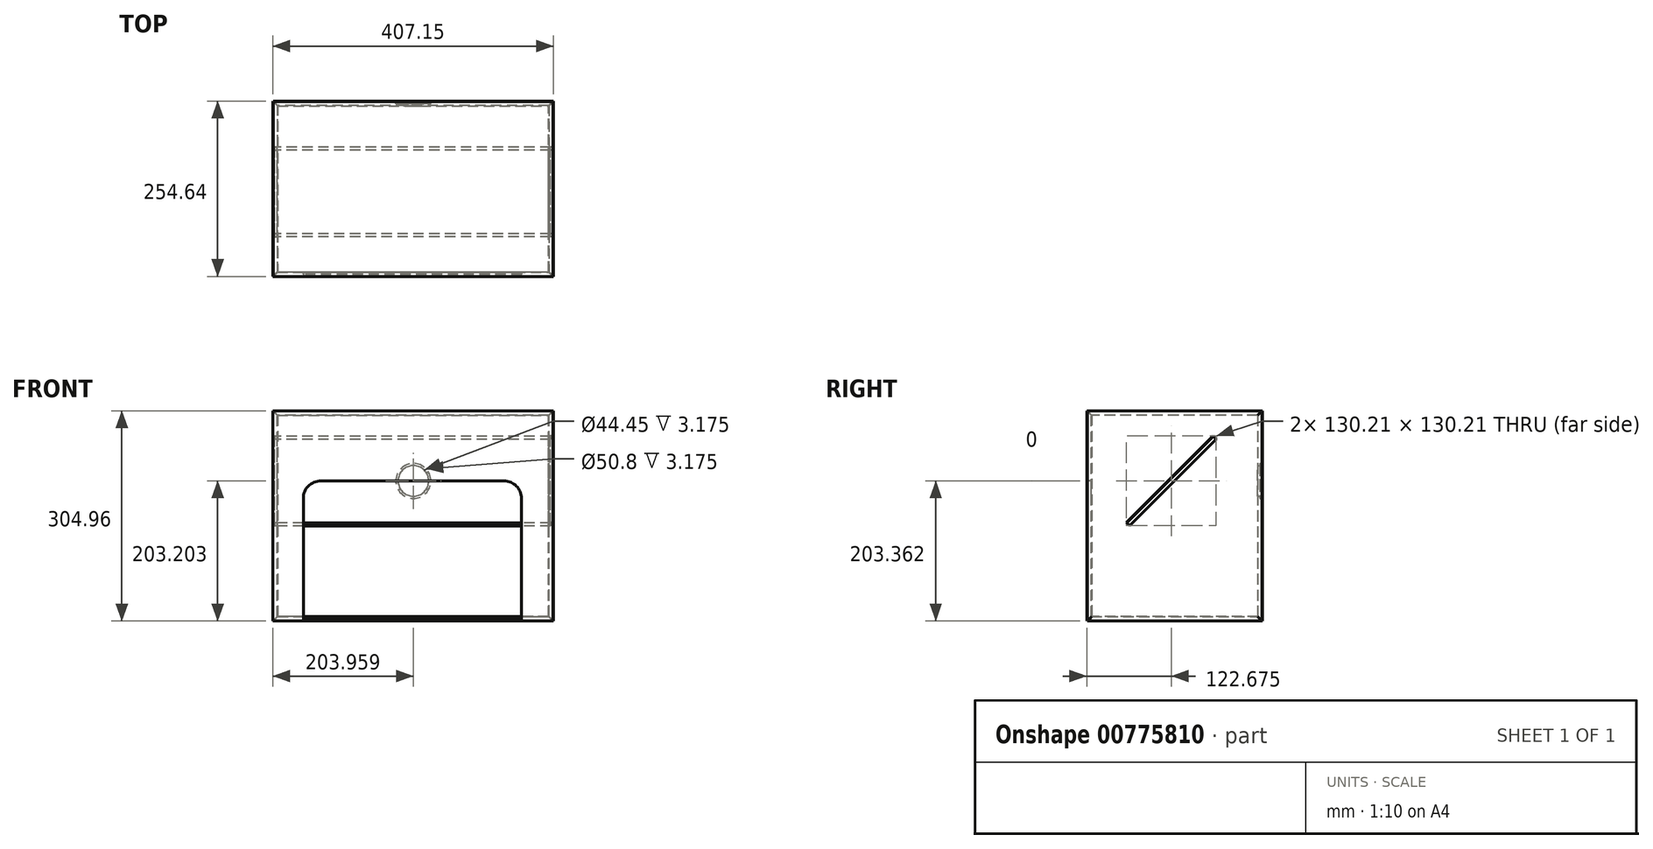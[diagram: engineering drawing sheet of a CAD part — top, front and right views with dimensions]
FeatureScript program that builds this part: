
annotation { "Feature Type Name" : "Feature", "Feature Type Description" : "" }
export const myFeature = defineFeature(function(context is Context, id is Id, definition is map)
    precondition{}
    {
        {
            var Q0;
            Q0=qCreatedBy(makeId("Top.planeOp"),FACE);
            var sketch = newSketch(context, id + "F0", { "sketchPlane" : qUnion([Q0])});
            skLineSegment(sketch, "E0.bottom", {"start": v(-199.1, 158) * mm, "end": v(207.3, 158) * mm});
            skLineSegment(sketch, "E0.top", {"start": v(-199.1, -96) * mm, "end": v(207.3, -96) * mm});
            skLineSegment(sketch, "E0.left", {"start": v(-199.1, 158) * mm, "end": v(-199.1, -96) * mm});
            skLineSegment(sketch, "E0.right", {"start": v(207.3, 158) * mm, "end": v(207.3, -96) * mm});
            skSolve(sketch);
        }
        {
            var Q0;
            Q0=makeQuery(id+"F0.imprint","IMPRINT",FACE,{"disambiguationData":[TD([[makeQuery(id+"F0.imprint","IMPRINT",EDGE,{"derivedFrom":sQuery(id+"F0.wireOp",EDGE,"E0.bottom")}),-1.0]])]});
            extrude(context, id + "F1", {"entities" : qUnion([Q0]), "depth" : 6.35 * mm, "offsetDistance" : 25.4 * mm});
        }
        {
            var Q0;
            Q0=makeQuery(id+"F1.opExtrude","CAP_EDGE",EDGE,{"disambiguationData":[OSD([sQuery(id+"F0.wireOp",EDGE,"E0.left")])],"isStart":false});
            var Q1;
            Q1=makeQuery(id+"F1.opExtrude","CAP_FACE",FACE,{"disambiguationData":[OSD([sQuery(id+"F0.wireOp",EDGE,"E0.bottom"),sQuery(id+"F0.wireOp",EDGE,"E0.top"),sQuery(id+"F0.wireOp",EDGE,"E0.left"),sQuery(id+"F0.wireOp",EDGE,"E0.right")])],"isStart":false});
            var Q2;
            Q2=makeQuery(id+"F1.opExtrude","CAP_EDGE",EDGE,{"disambiguationData":[OSD([sQuery(id+"F0.wireOp",EDGE,"E0.bottom")])],"isStart":false});
            var Q3;
            Q3=makeQuery(id+"F1.opExtrude","CAP_EDGE",EDGE,{"disambiguationData":[OSD([sQuery(id+"F0.wireOp",EDGE,"E0.right")])],"isStart":false});
            chamfer(context, id + "F2", {"entities" : qUnion([Q0, Q1, Q2, Q3]), "width" : 6.35 * mm, "tangentPropagation" : true});
        }
        {
            var Q0;
            Q0=qCreatedBy(makeId("Front.planeOp"),FACE);
            var sketch = newSketch(context, id + "F3", { "sketchPlane" : qUnion([Q0])});
            skLineSegment(sketch, "E1.bottom", {"start": v(-118.82, 429.1) * mm, "end": v(287.58, 429.1) * mm});
            skLineSegment(sketch, "E1.top", {"start": v(-118.82, 124.3) * mm, "end": v(287.58, 124.3) * mm});
            skLineSegment(sketch, "E1.left", {"start": v(-118.82, 429.1) * mm, "end": v(-118.82, 124.3) * mm});
            skLineSegment(sketch, "E1.right", {"start": v(287.58, 429.1) * mm, "end": v(287.58, 124.3) * mm});
            skSolve(sketch);
        }
        {
            var Q0;
            Q0=makeQuery(id+"F3.imprint","IMPRINT",FACE,{"disambiguationData":[TD([[makeQuery(id+"F3.imprint","IMPRINT",EDGE,{"derivedFrom":sQuery(id+"F3.wireOp",EDGE,"E1.bottom")}),-1.0]])]});
            extrude(context, id + "F4", {"entities" : qUnion([Q0]), "depth" : 6.35 * mm, "offsetDistance" : 25.4 * mm});
        }
        {
            var Q0;
            Q0=makeQuery(id+"F4.opExtrude","CAP_EDGE",EDGE,{"disambiguationData":[OSD([sQuery(id+"F3.wireOp",EDGE,"E1.top")])],"isStart":false});
            var Q1;
            Q1=makeQuery(id+"F4.opExtrude","CAP_EDGE",EDGE,{"disambiguationData":[OSD([sQuery(id+"F3.wireOp",EDGE,"E1.right")])],"isStart":false});
            var Q2;
            Q2=makeQuery(id+"F4.opExtrude","CAP_EDGE",EDGE,{"disambiguationData":[OSD([sQuery(id+"F3.wireOp",EDGE,"E1.left")])],"isStart":false});
            var Q3;
            Q3=makeQuery(id+"F4.opExtrude","CAP_EDGE",EDGE,{"disambiguationData":[OSD([sQuery(id+"F3.wireOp",EDGE,"E1.bottom")])],"isStart":false});
            chamfer(context, id + "F5", {"entities" : qUnion([Q0, Q1, Q2, Q3]), "width" : 6.35 * mm, "tangentPropagation" : true});
        }
        {
            var Q0;
            Q0=makeQuery(id+"F4.opExtrude","CAP_FACE",FACE,{"disambiguationData":[OSD([sQuery(id+"F3.wireOp",EDGE,"E1.bottom"),sQuery(id+"F3.wireOp",EDGE,"E1.top"),sQuery(id+"F3.wireOp",EDGE,"E1.left"),sQuery(id+"F3.wireOp",EDGE,"E1.right")])],"isStart":true});
            var sketch = newSketch(context, id + "F6", { "sketchPlane" : qUnion([Q0])});
            skPoint(sketch, "E2", {"position": v(-84.39, 327.5) * mm});
            skSolve(sketch);
        }
        {
            var Q0;
            Q0=sQuery(id+"F6.wireOp",VERTEX,"E2");
            var Q1;
            Q1=makeQuery(id+"F4.opExtrude","SWEPT_BODY",BODY,{"disambiguationData":[OSD([sQuery(id+"F3.wireOp",EDGE,"E1.bottom"),sQuery(id+"F3.wireOp",EDGE,"E1.top"),sQuery(id+"F3.wireOp",EDGE,"E1.left"),sQuery(id+"F3.wireOp",EDGE,"E1.right")])]});
            hole(context, id + "F7", {"style" : HoleStyle.C_BORE, "endStyle" : HoleEndStyle.THROUGH, "holeDiameter" : 44.45 * mm, "cBoreDiameter" : 50.8 * mm, "cBoreDepth" : 3.17 * mm, "majorDiameter" : 6.35 * mm, "isTappedThrough" : true, "tappedDepth" : 12.7 * mm, "tapClearance" : 3, "locations" : qUnion([Q0]), "scope" : qUnion([Q1])});
        }
        {
            var Q0;
            Q0=qCreatedBy(makeId("Right.planeOp"),FACE);
            var sketch = newSketch(context, id + "F8", { "sketchPlane" : qUnion([Q0])});
            skLineSegment(sketch, "E3.bottom", {"start": v(-236.32, 132.56) * mm, "end": v(-43.57, 132.56) * mm});
            skLineSegment(sketch, "E3.top", {"start": v(-236.32, 138.95) * mm, "end": v(-43.57, 138.95) * mm});
            skLineSegment(sketch, "E3.left", {"start": v(-236.32, 132.56) * mm, "end": v(-236.32, 138.95) * mm});
            skLineSegment(sketch, "E3.right", {"start": v(-43.57, 132.56) * mm, "end": v(-43.57, 138.95) * mm});
            skSolve(sketch);
        }
        {
            var Q0;
            Q0 = qSketchRegion(id + "F8", true);
            extrude(context, id + "F9", {"entities" : qUnion([Q0]), "depth" : 355.6 * mm, "offsetDistance" : 25.4 * mm});
        }
        {
            var Q0;
            Q0=makeQuery(id+"F9.opExtrude","SWEPT_BODY",BODY,{"disambiguationData":[OSD([sQuery(id+"F8.wireOp",EDGE,"E3.bottom"),sQuery(id+"F8.wireOp",EDGE,"E3.top"),sQuery(id+"F8.wireOp",EDGE,"E3.left"),sQuery(id+"F8.wireOp",EDGE,"E3.right")])]});
            var Q1;
            Q1=makeQuery(id+"F9.opExtrude","SWEPT_EDGE",EDGE,{"disambiguationData":[OSD([sQuery(id+"F8.wireOp",EDGE,"E3.bottom"),sQuery(id+"F8.wireOp",EDGE,"E3.left")])]});
            transform(context, id + "F10", {"entities" : qUnion([Q0]), "transformType" : TransformType.ROTATION, "transformAxis" : qUnion([Q1]), "angle" : 45 * degree, "oppositeDirection" : true, "makeCopy" : false});
        }
        {
            var Q0;
            Q0=makeQuery(id+"F9.opExtrude","SWEPT_BODY",BODY,{"disambiguationData":[OSD([sQuery(id+"F8.wireOp",EDGE,"E3.bottom"),sQuery(id+"F8.wireOp",EDGE,"E3.top"),sQuery(id+"F8.wireOp",EDGE,"E3.left"),sQuery(id+"F8.wireOp",EDGE,"E3.right")])]});
            var Q1;
            Q1=qCreatedBy(makeId("Right.planeOp"),FACE);
            transform(context, id + "F11", {"entities" : qUnion([Q0]), "transformType" : TransformType.TRANSLATION_DISTANCE, "transformDirection" : qUnion([Q1]), "distance" : 101.6 * mm, "oppositeDirection" : true, "makeCopy" : false});
        }
        {
            var Q0;
            Q0=makeQuery(id+"F9.opExtrude","SWEPT_BODY",BODY,{"disambiguationData":[OSD([sQuery(id+"F8.wireOp",EDGE,"E3.bottom"),sQuery(id+"F8.wireOp",EDGE,"E3.top"),sQuery(id+"F8.wireOp",EDGE,"E3.left"),sQuery(id+"F8.wireOp",EDGE,"E3.right")])]});
            var Q1;
            Q1=makeQuery(id+"F9.opExtrude","SWEPT_FACE",FACE,{"disambiguationData":[OSD([sQuery(id+"F8.wireOp",EDGE,"E3.top")])]});
            transform(context, id + "F12", {"entities" : qUnion([Q0]), "transformType" : TransformType.TRANSLATION_DISTANCE, "transformDirection" : qUnion([Q1]), "distance" : 101.6 * mm, "makeCopy" : false});
        }
        {
            var Q0;
            Q0=makeQuery(id+"F9.opExtrude","CAP_EDGE",EDGE,{"disambiguationData":[OSD([sQuery(id+"F8.wireOp",EDGE,"E3.bottom")])],"isStart":false});
            var Q1;
            Q1=makeQuery(id+"F9.opExtrude","CAP_EDGE",EDGE,{"disambiguationData":[OSD([sQuery(id+"F8.wireOp",EDGE,"E3.top")])],"isStart":false});
            chamfer(context, id + "F13", {"entities" : qUnion([Q0, Q1]), "width" : 2.54 * mm, "tangentPropagation" : true});
        }
        {
            var Q0;
            Q0=makeQuery(id+"F4.opExtrude","SWEPT_BODY",BODY,{"disambiguationData":[OSD([sQuery(id+"F3.wireOp",EDGE,"E1.bottom"),sQuery(id+"F3.wireOp",EDGE,"E1.top"),sQuery(id+"F3.wireOp",EDGE,"E1.left"),sQuery(id+"F3.wireOp",EDGE,"E1.right")])]});
            transform(context, id + "F14", {"entities" : qUnion([Q0]), "transformType" : TransformType.TRANSLATION_3D, "dx" : 0 * mm, "dy" : 152.4 * mm, "dz" : -127 * mm, "makeCopy" : false});
        }
        {
            var Q0;
            Q0=makeQuery(id+"F1.opExtrude","SWEPT_BODY",BODY,{"disambiguationData":[OSD([sQuery(id+"F0.wireOp",EDGE,"E0.bottom"),sQuery(id+"F0.wireOp",EDGE,"E0.top"),sQuery(id+"F0.wireOp",EDGE,"E0.left"),sQuery(id+"F0.wireOp",EDGE,"E0.right")])]});
            transform(context, id + "F15", {"entities" : qUnion([Q0]), "transformType" : TransformType.TRANSLATION_3D, "dx" : 0 * mm, "dy" : -5.08 * mm, "dz" : -2.54 * mm, "makeCopy" : false});
        }
        {
            var Q0;
            Q0=makeQuery(id+"F4.opExtrude","SWEPT_BODY",BODY,{"disambiguationData":[OSD([sQuery(id+"F3.wireOp",EDGE,"E1.bottom"),sQuery(id+"F3.wireOp",EDGE,"E1.top"),sQuery(id+"F3.wireOp",EDGE,"E1.left"),sQuery(id+"F3.wireOp",EDGE,"E1.right")])]});
            transform(context, id + "F16", {"entities" : qUnion([Q0]), "transformType" : TransformType.TRANSLATION_3D, "dx" : -80 * mm, "dy" : 0 * mm, "dz" : 0 * mm, "makeCopy" : false});
        }
        {
            var Q0;
            Q0=qCreatedBy(makeId("Right.planeOp"),FACE);
            var sketch = newSketch(context, id + "F17", { "sketchPlane" : qUnion([Q0])});
            skLineSegment(sketch, "E4.bottom", {"start": v(153.04, 0) * mm, "end": v(-100.96, 0) * mm});
            skLineSegment(sketch, "E4.top", {"start": v(153.04, 304.8) * mm, "end": v(-100.96, 304.8) * mm});
            skLineSegment(sketch, "E4.left", {"start": v(153.04, 0) * mm, "end": v(153.04, 304.8) * mm});
            skLineSegment(sketch, "E4.right", {"start": v(-100.96, 0) * mm, "end": v(-100.96, 304.8) * mm});
            skSolve(sketch);
        }
        {
            var Q0;
            Q0=makeQuery(id+"F17.imprint","IMPRINT",FACE,{"disambiguationData":[TD([[makeQuery(id+"F17.imprint","IMPRINT",EDGE,{"derivedFrom":sQuery(id+"F17.wireOp",EDGE,"E4.bottom")}),-1.0]])]});
            extrude(context, id + "F18", {"entities" : qUnion([Q0]), "depth" : 6.35 * mm, "offsetDistance" : 25.4 * mm});
        }
        {
            var Q0;
            Q0=makeQuery(id+"F18.opExtrude","SWEPT_BODY",BODY,{"disambiguationData":[OSD([sQuery(id+"F17.wireOp",EDGE,"E4.bottom"),sQuery(id+"F17.wireOp",EDGE,"E4.top"),sQuery(id+"F17.wireOp",EDGE,"E4.left"),sQuery(id+"F17.wireOp",EDGE,"E4.right")])]});
            transform(context, id + "F19", {"entities" : qUnion([Q0]), "transformType" : TransformType.TRANSLATION_3D, "dx" : -199.39 * mm, "dy" : 0 * mm, "dz" : -2.54 * mm, "makeCopy" : false});
        }
        {
            var Q0;
            Q0=makeQuery(id+"F18.opExtrude","CAP_EDGE",EDGE,{"disambiguationData":[OSD([sQuery(id+"F17.wireOp",EDGE,"E4.bottom")])],"isStart":false});
            var Q1;
            Q1=makeQuery(id+"F18.opExtrude","CAP_EDGE",EDGE,{"disambiguationData":[OSD([sQuery(id+"F17.wireOp",EDGE,"E4.right")])],"isStart":false});
            var Q2;
            Q2=makeQuery(id+"F18.opExtrude","CAP_EDGE",EDGE,{"disambiguationData":[OSD([sQuery(id+"F17.wireOp",EDGE,"E4.left")])],"isStart":false});
            var Q3;
            Q3=makeQuery(id+"F18.opExtrude","CAP_EDGE",EDGE,{"disambiguationData":[OSD([sQuery(id+"F17.wireOp",EDGE,"E4.top")])],"isStart":false});
            chamfer(context, id + "F20", {"entities" : qUnion([Q0, Q1, Q2, Q3]), "width" : 6.35 * mm, "tangentPropagation" : true});
        }
        {
            var Q0;
            Q0=qCreatedBy(makeId("Right.planeOp"),FACE);
            var sketch = newSketch(context, id + "F21", { "sketchPlane" : qUnion([Q0])});
            skLineSegment(sketch, "E5.bottom", {"start": v(-47.49, 150.59) * mm, "end": v(78.24, 276.31) * mm});
            skLineSegment(sketch, "E5.top", {"start": v(-43, 146.1) * mm, "end": v(82.73, 271.82) * mm});
            skLineSegment(sketch, "E5.left", {"start": v(-47.49, 150.59) * mm, "end": v(-43, 146.1) * mm});
            skLineSegment(sketch, "E5.right", {"start": v(78.24, 276.31) * mm, "end": v(82.73, 271.82) * mm});
            skSolve(sketch);
        }
        {
            var Q0;
            Q0 = qSketchRegion(id + "F21", true);
            extrude(context, id + "F22", {"entities" : qUnion([Q0]), "depth" : 400.05 * mm, "offsetDistance" : 25.4 * mm});
        }
        {
            var Q0;
            Q0=makeQuery(id+"F18.opExtrude","CAP_FACE",FACE,{"disambiguationData":[OSD([sQuery(id+"F17.wireOp",EDGE,"E4.bottom"),sQuery(id+"F17.wireOp",EDGE,"E4.top"),sQuery(id+"F17.wireOp",EDGE,"E4.left"),sQuery(id+"F17.wireOp",EDGE,"E4.right")])],"isStart":false});
            var sketch = newSketch(context, id + "F23", { "sketchPlane" : qUnion([Q0])});
            skLineSegment(sketch, "E6.bottom", {"start": v(-44.03, 140.05) * mm, "end": v(81.7, 265.77) * mm});
            skLineSegment(sketch, "E6.top", {"start": v(-39.54, 135.56) * mm, "end": v(86.18, 261.28) * mm});
            skLineSegment(sketch, "E6.left", {"start": v(-44.03, 140.05) * mm, "end": v(-39.54, 135.56) * mm});
            skLineSegment(sketch, "E6.right", {"start": v(81.7, 265.77) * mm, "end": v(86.18, 261.28) * mm});
            skSolve(sketch);
        }
        {
            var Q0;
            Q0 = qSketchRegion(id + "F23", true);
            extrude(context, id + "F24", {"entities" : qUnion([Q0]), "operationType" : NewBodyOperationType.REMOVE, "oppositeDirection" : true, "depth" : 3.17 * mm, "offsetDistance" : 25.4 * mm});
        }
        {
            var Q0;
            Q0=makeQuery(id+"F22.opExtrude","SWEPT_FACE",FACE,{"disambiguationData":[OSD([sQuery(id+"F21.wireOp",EDGE,"E5.top")])]});
            var sketch = newSketch(context, id + "F25", { "sketchPlane" : qUnion([Q0])});
            skLineSegment(sketch, "E7.bottom", {"start": v(25.4, -98.32) * mm, "end": v(374.65, -98.32) * mm});
            skLineSegment(sketch, "E7.top", {"start": v(25.4, -225.32) * mm, "end": v(374.65, -225.32) * mm});
            skLineSegment(sketch, "E7.left", {"start": v(25.4, -98.32) * mm, "end": v(25.4, -225.32) * mm});
            skLineSegment(sketch, "E7.right", {"start": v(374.65, -98.32) * mm, "end": v(374.65, -225.32) * mm});
            skPoint(sketch, "E7.middle", {"position": v(207.97, -188.2) * mm});
            skSolve(sketch);
        }
        {
            var Q0;
            Q0=makeQuery(id+"F25.imprint","IMPRINT",FACE,{"disambiguationData":[TD([[makeQuery(id+"F25.imprint","IMPRINT",EDGE,{"derivedFrom":sQuery(id+"F25.wireOp",EDGE,"E7.bottom")}),-1.0]])]});
            extrude(context, id + "F26", {"entities" : qUnion([Q0]), "operationType" : NewBodyOperationType.REMOVE, "oppositeDirection" : true, "depth" : 3.17 * mm, "offsetDistance" : 25.4 * mm});
        }
        {
            var Q0;
            Q0=makeQuery(id+"F18.opExtrude","SWEPT_BODY",BODY,{"disambiguationData":[OSD([sQuery(id+"F17.wireOp",EDGE,"E4.bottom"),sQuery(id+"F17.wireOp",EDGE,"E4.top"),sQuery(id+"F17.wireOp",EDGE,"E4.left"),sQuery(id+"F17.wireOp",EDGE,"E4.right")])]});
            transform(context, id + "F27", {"entities" : qUnion([Q0]), "transformType" : TransformType.TRANSLATION_3D, "dx" : 0 * mm, "dy" : 0 * mm, "dz" : 0 * mm, "makeCopy" : true});
        }
        {
            var Q0;
            Q0=makeQuery(id+"F27.opPattern","COPY",BODY,{"derivedFrom":makeQuery(id+"F18.opExtrude","SWEPT_BODY",BODY,{"disambiguationData":[OSD([sQuery(id+"F17.wireOp",EDGE,"E4.bottom"),sQuery(id+"F17.wireOp",EDGE,"E4.top"),sQuery(id+"F17.wireOp",EDGE,"E4.left"),sQuery(id+"F17.wireOp",EDGE,"E4.right")])]}),"instanceName":"1"});
            deleteBodies(context, id + "F28", {"entities" : qUnion([Q0])});
        }
        {
            var Q0;
            Q0 = qSketchRegion(id + "F23", true);
            extrude(context, id + "F29", {"entities" : qUnion([Q0]), "operationType" : NewBodyOperationType.REMOVE, "oppositeDirection" : true, "depth" : 25.4 * mm, "offsetDistance" : 25.4 * mm});
        }
        {
            var Q0;
            Q0=qCreatedBy(makeId("Front.planeOp"),FACE);
            var sketch = newSketch(context, id + "F30", { "sketchPlane" : qUnion([Q0])});
            skLineSegment(sketch, "E8.bottom", {"start": v(209.36, 0) * mm, "end": v(-197.04, 0) * mm});
            skLineSegment(sketch, "E8.top", {"start": v(209.36, 304.8) * mm, "end": v(-197.04, 304.8) * mm});
            skLineSegment(sketch, "E8.left", {"start": v(209.36, 0) * mm, "end": v(209.36, 304.8) * mm});
            skLineSegment(sketch, "E8.right", {"start": v(-197.04, 0) * mm, "end": v(-197.04, 304.8) * mm});
            skSolve(sketch);
        }
        {
            var Q0;
            Q0=makeQuery(id+"F30.imprint","IMPRINT",FACE,{"disambiguationData":[TD([[makeQuery(id+"F30.imprint","IMPRINT",EDGE,{"derivedFrom":sQuery(id+"F30.wireOp",EDGE,"E8.bottom")}),-1.0]])]});
            extrude(context, id + "F31", {"entities" : qUnion([Q0]), "depth" : 6.35 * mm, "offsetDistance" : 25.4 * mm});
        }
        {
            var Q0;
            Q0=makeQuery(id+"F31.opExtrude","CAP_EDGE",EDGE,{"disambiguationData":[OSD([sQuery(id+"F30.wireOp",EDGE,"E8.left")])],"isStart":true});
            var Q1;
            Q1=makeQuery(id+"F31.opExtrude","CAP_EDGE",EDGE,{"disambiguationData":[OSD([sQuery(id+"F30.wireOp",EDGE,"E8.bottom")])],"isStart":true});
            var Q2;
            Q2=makeQuery(id+"F31.opExtrude","CAP_EDGE",EDGE,{"disambiguationData":[OSD([sQuery(id+"F30.wireOp",EDGE,"E8.right")])],"isStart":true});
            var Q3;
            Q3=makeQuery(id+"F31.opExtrude","CAP_EDGE",EDGE,{"disambiguationData":[OSD([sQuery(id+"F30.wireOp",EDGE,"E8.top")])],"isStart":true});
            chamfer(context, id + "F32", {"entities" : qUnion([Q0, Q1, Q2, Q3]), "width" : 6.35 * mm, "tangentPropagation" : true});
        }
        {
            var Q0;
            Q0=makeQuery(id+"F31.opExtrude","SWEPT_BODY",BODY,{"disambiguationData":[OSD([sQuery(id+"F30.wireOp",EDGE,"E8.bottom"),sQuery(id+"F30.wireOp",EDGE,"E8.top"),sQuery(id+"F30.wireOp",EDGE,"E8.left"),sQuery(id+"F30.wireOp",EDGE,"E8.right")])]});
            transform(context, id + "F33", {"entities" : qUnion([Q0]), "transformType" : TransformType.TRANSLATION_3D, "dx" : -2.54 * mm, "dy" : -95.25 * mm, "dz" : 0 * mm, "makeCopy" : false});
        }
        {
            var Q0;
            Q0=makeQuery(id+"F31.opExtrude","CAP_FACE",FACE,{"disambiguationData":[OSD([sQuery(id+"F30.wireOp",EDGE,"E8.bottom"),sQuery(id+"F30.wireOp",EDGE,"E8.top"),sQuery(id+"F30.wireOp",EDGE,"E8.left"),sQuery(id+"F30.wireOp",EDGE,"E8.right")])],"isStart":false});
            var sketch = newSketch(context, id + "F34", { "sketchPlane" : qUnion([Q0])});
            skLineSegment(sketch, "E9", {"start": v(-155.34, 0) * mm, "end": v(-155.34, 177.8) * mm});
            skLineSegment(sketch, "E10", {"start": v(161.17, 177.8) * mm, "end": v(161.17, 0) * mm});
            skLineSegment(sketch, "E11", {"start": v(161.17, 0) * mm, "end": v(-155.34, 0) * mm});
            skLineSegment(sketch, "E12", {"start": v(-129.94, 203.2) * mm, "end": v(135.77, 203.2) * mm});
            skPoint(sketch, "E13.visualSharp", {"position": v(-155.34, 203.2) * mm});
            skArc(sketch, "E13.filletArc", {"start": v(-129.94, 203.2) * mm, "mid": v(-147.9, 195.76) * mm, "end": v(-155.34, 177.8) * mm});
            skPoint(sketch, "E14.visualSharp", {"position": v(161.17, 203.2) * mm});
            skArc(sketch, "E14.filletArc", {"start": v(161.17, 177.8) * mm, "mid": v(153.73, 195.76) * mm, "end": v(135.77, 203.2) * mm});
            skSolve(sketch);
        }
        {
            var Q0;
            Q0=makeQuery(id+"F34.imprint","IMPRINT",FACE,{"disambiguationData":[TD([[makeQuery(id+"F34.imprint","IMPRINT",EDGE,{"derivedFrom":sQuery(id+"F34.wireOp",EDGE,"E9")}),-1.0]])]});
            extrude(context, id + "F35", {"entities" : qUnion([Q0]), "operationType" : NewBodyOperationType.REMOVE, "oppositeDirection" : true, "depth" : 6.35 * mm, "offsetDistance" : 25.4 * mm});
        }
        {
            var Q0;
            Q0=makeQuery(id+"F9.opExtrude","SWEPT_BODY",BODY,{"disambiguationData":[OSD([sQuery(id+"F8.wireOp",EDGE,"E3.bottom"),sQuery(id+"F8.wireOp",EDGE,"E3.top"),sQuery(id+"F8.wireOp",EDGE,"E3.left"),sQuery(id+"F8.wireOp",EDGE,"E3.right")])]});
            deleteBodies(context, id + "F36", {"entities" : qUnion([Q0])});
        }
        {
            var Q0;
            Q0=makeQuery(id+"F22.opExtrude","SWEPT_BODY",BODY,{"disambiguationData":[OSD([sQuery(id+"F21.wireOp",EDGE,"E5.bottom"),sQuery(id+"F21.wireOp",EDGE,"E5.top"),sQuery(id+"F21.wireOp",EDGE,"E5.left"),sQuery(id+"F21.wireOp",EDGE,"E5.right")])]});
            transform(context, id + "F37", {"entities" : qUnion([Q0]), "transformType" : TransformType.TRANSLATION_3D, "dx" : -196.85 * mm, "dy" : 3.56 * mm, "dz" : -11.18 * mm, "makeCopy" : false});
        }
        {
            var Q0;
            Q0=makeQuery(id+"F31.opExtrude","SWEPT_BODY",BODY,{"disambiguationData":[OSD([sQuery(id+"F30.wireOp",EDGE,"E8.bottom"),sQuery(id+"F30.wireOp",EDGE,"E8.top"),sQuery(id+"F30.wireOp",EDGE,"E8.left"),sQuery(id+"F30.wireOp",EDGE,"E8.right")])]});
            transform(context, id + "F38", {"entities" : qUnion([Q0]), "transformType" : TransformType.TRANSLATION_3D, "dx" : 0 * mm, "dy" : 0 * mm, "dz" : -2.54 * mm, "makeCopy" : false});
        }
        {
            var Q0;
            Q0=qCreatedBy(makeId("Top.planeOp"),FACE);
            var sketch = newSketch(context, id + "F39", { "sketchPlane" : qUnion([Q0])});
            skLineSegment(sketch, "E15.bottom", {"start": v(-198.61, 151.65) * mm, "end": v(207.79, 151.65) * mm});
            skLineSegment(sketch, "E15.top", {"start": v(-198.61, -102.35) * mm, "end": v(207.79, -102.35) * mm});
            skLineSegment(sketch, "E15.left", {"start": v(-198.61, 151.65) * mm, "end": v(-198.61, -102.35) * mm});
            skLineSegment(sketch, "E15.right", {"start": v(207.79, 151.65) * mm, "end": v(207.79, -102.35) * mm});
            skSolve(sketch);
        }
        {
            var Q0;
            Q0 = qSketchRegion(id + "F39", true);
            extrude(context, id + "F40", {"entities" : qUnion([Q0]), "depth" : 6.35 * mm, "offsetDistance" : 25.4 * mm});
        }
        {
            var Q0;
            Q0=makeQuery(id+"F40.opExtrude","SWEPT_BODY",BODY,{"disambiguationData":[OSD([sQuery(id+"F39.wireOp",EDGE,"E15.bottom"),sQuery(id+"F39.wireOp",EDGE,"E15.top"),sQuery(id+"F39.wireOp",EDGE,"E15.left"),sQuery(id+"F39.wireOp",EDGE,"E15.right")])]});
            transform(context, id + "F41", {"entities" : qUnion([Q0]), "transformType" : TransformType.TRANSLATION_3D, "dx" : 0 * mm, "dy" : 1.27 * mm, "dz" : 295.9 * mm, "makeCopy" : false});
        }
        {
            var Q0;
            Q0=makeQuery(id+"F40.opExtrude","SWEPT_BODY",BODY,{"disambiguationData":[OSD([sQuery(id+"F39.wireOp",EDGE,"E15.bottom"),sQuery(id+"F39.wireOp",EDGE,"E15.top"),sQuery(id+"F39.wireOp",EDGE,"E15.left"),sQuery(id+"F39.wireOp",EDGE,"E15.right")])]});
            deleteBodies(context, id + "F42", {"entities" : qUnion([Q0])});
        }
        {
            var Q0;
            Q0=qCreatedBy(makeId("Top.planeOp"),FACE);
            var sketch = newSketch(context, id + "F43", { "sketchPlane" : qUnion([Q0])});
            skLineSegment(sketch, "E16.bottom", {"start": v(-198.98, 153.46) * mm, "end": v(207.42, 153.46) * mm});
            skLineSegment(sketch, "E16.top", {"start": v(-198.98, -100.54) * mm, "end": v(207.42, -100.54) * mm});
            skLineSegment(sketch, "E16.left", {"start": v(-198.98, 153.46) * mm, "end": v(-198.98, -100.54) * mm});
            skLineSegment(sketch, "E16.right", {"start": v(207.42, 153.46) * mm, "end": v(207.42, -100.54) * mm});
            skSolve(sketch);
        }
        {
            var Q0;
            Q0 = qSketchRegion(id + "F43", true);
            extrude(context, id + "F44", {"entities" : qUnion([Q0]), "depth" : 6.35 * mm, "offsetDistance" : 25.4 * mm});
        }
        {
            var Q0;
            Q0=makeQuery(id+"F44.opExtrude","SWEPT_BODY",BODY,{"disambiguationData":[OSD([sQuery(id+"F43.wireOp",EDGE,"E16.bottom"),sQuery(id+"F43.wireOp",EDGE,"E16.top"),sQuery(id+"F43.wireOp",EDGE,"E16.left"),sQuery(id+"F43.wireOp",EDGE,"E16.right")])]});
            transform(context, id + "F45", {"entities" : qUnion([Q0]), "transformType" : TransformType.TRANSLATION_3D, "dx" : 0 * mm, "dy" : -1.02 * mm, "dz" : 295.9 * mm, "makeCopy" : false});
        }
        {
            var Q0;
            Q0=makeQuery(id+"F44.opExtrude","CAP_EDGE",EDGE,{"disambiguationData":[OSD([sQuery(id+"F43.wireOp",EDGE,"E16.top")])],"isStart":true});
            var Q1;
            Q1=makeQuery(id+"F44.opExtrude","CAP_EDGE",EDGE,{"disambiguationData":[OSD([sQuery(id+"F43.wireOp",EDGE,"E16.left")])],"isStart":true});
            var Q2;
            Q2=makeQuery(id+"F44.opExtrude","CAP_EDGE",EDGE,{"disambiguationData":[OSD([sQuery(id+"F43.wireOp",EDGE,"E16.bottom")])],"isStart":true});
            var Q3;
            Q3=makeQuery(id+"F44.opExtrude","CAP_EDGE",EDGE,{"disambiguationData":[OSD([sQuery(id+"F43.wireOp",EDGE,"E16.right")])],"isStart":true});
            chamfer(context, id + "F46", {"entities" : qUnion([Q0, Q1, Q2, Q3]), "width" : 6.35 * mm, "tangentPropagation" : true});
        }
        {
            var Q0;
            Q0=makeQuery(id+"F18.opExtrude","SWEPT_BODY",BODY,{"disambiguationData":[OSD([sQuery(id+"F17.wireOp",EDGE,"E4.bottom"),sQuery(id+"F17.wireOp",EDGE,"E4.top"),sQuery(id+"F17.wireOp",EDGE,"E4.left"),sQuery(id+"F17.wireOp",EDGE,"E4.right")])]});
            var Q1;
            Q1=qCreatedBy(makeId("Right.planeOp"),FACE);
            mirror(context, id + "F47", {"entities" : qUnion([Q0]), "mirrorPlane" : qUnion([Q1])});
        }
        {
            var Q0;
            Q0=makeQuery(id+"F47.opPattern","COPY",BODY,{"derivedFrom":makeQuery(id+"F18.opExtrude","SWEPT_BODY",BODY,{"disambiguationData":[OSD([sQuery(id+"F17.wireOp",EDGE,"E4.bottom"),sQuery(id+"F17.wireOp",EDGE,"E4.top"),sQuery(id+"F17.wireOp",EDGE,"E4.left"),sQuery(id+"F17.wireOp",EDGE,"E4.right")])]}),"instanceName":"1"});
            transform(context, id + "F48", {"entities" : qUnion([Q0]), "transformType" : TransformType.TRANSLATION_3D, "dx" : 0 * mm, "dy" : 0 * mm, "dz" : 0 * mm, "makeCopy" : false});
        }
        {
            var Q0;
            Q0=makeQuery(id+"F47.opPattern","COPY",BODY,{"derivedFrom":makeQuery(id+"F18.opExtrude","SWEPT_BODY",BODY,{"disambiguationData":[OSD([sQuery(id+"F17.wireOp",EDGE,"E4.bottom"),sQuery(id+"F17.wireOp",EDGE,"E4.top"),sQuery(id+"F17.wireOp",EDGE,"E4.left"),sQuery(id+"F17.wireOp",EDGE,"E4.right")])]}),"instanceName":"1"});
            transform(context, id + "F49", {"entities" : qUnion([Q0]), "transformType" : TransformType.TRANSLATION_3D, "dx" : 7.62 * mm, "dy" : 0 * mm, "dz" : 0 * mm, "makeCopy" : false});
        }
    });
